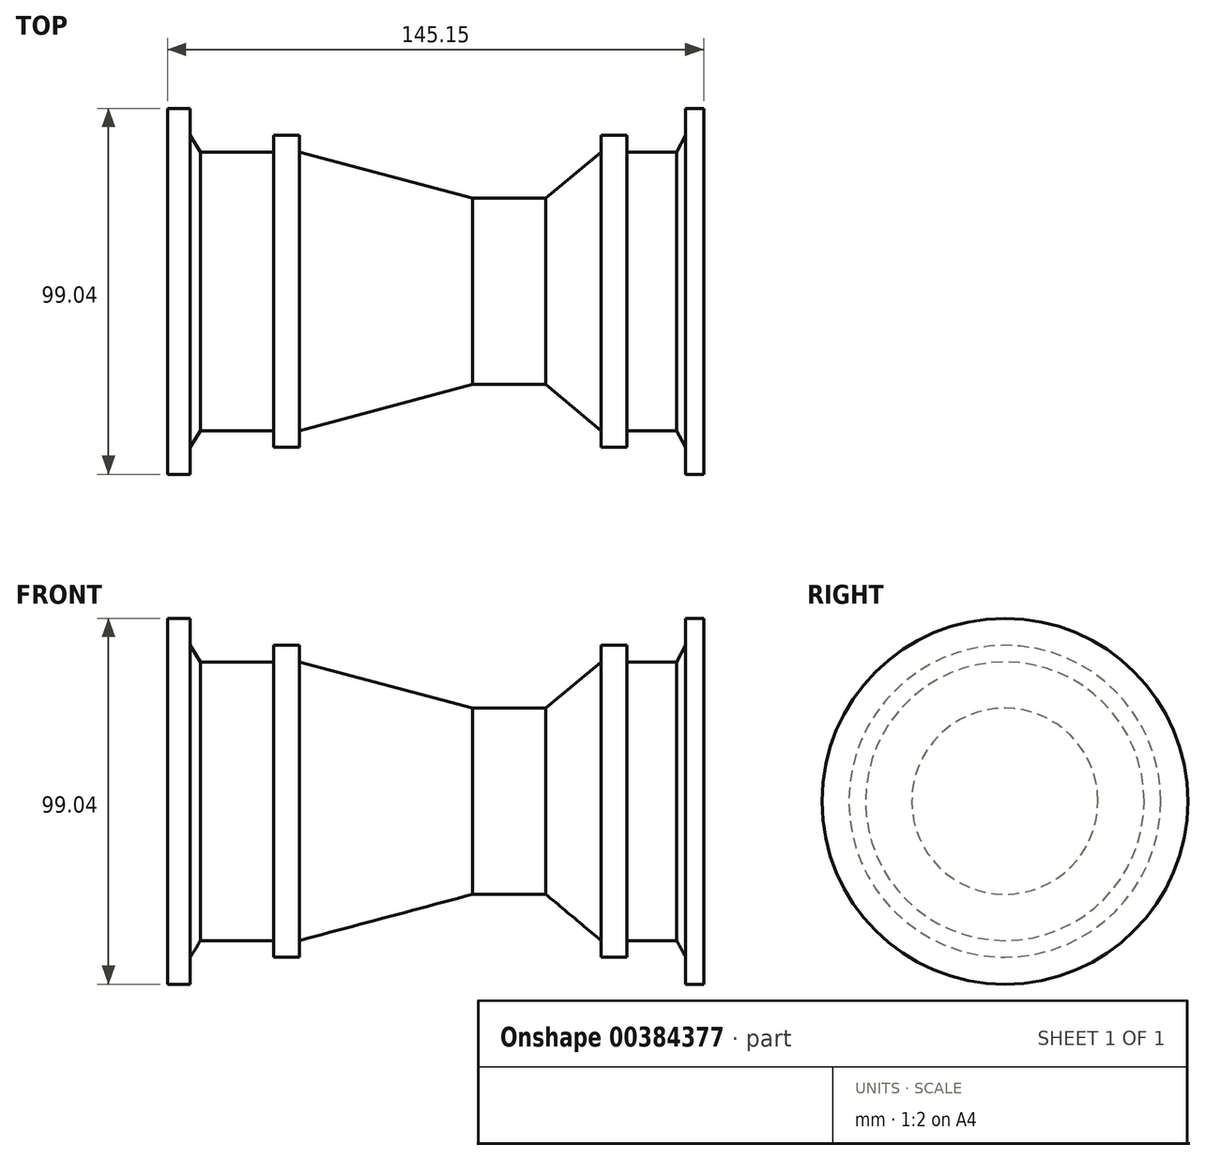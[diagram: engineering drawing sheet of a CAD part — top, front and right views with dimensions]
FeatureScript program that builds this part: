
annotation { "Feature Type Name" : "Feature", "Feature Type Description" : "" }
export const myFeature = defineFeature(function(context is Context, id is Id, definition is map)
    precondition{}
    {
        {
            var Q0;
            Q0=qCreatedBy(makeId("Front.planeOp"),FACE);
            var sketch = newSketch(context, id + "F0", { "sketchPlane" : qUnion([Q0])});
            skLineSegment(sketch, "E0", {"start": v(-72.5, 49.52) * mm, "end": v(-66.34, 49.52) * mm});
            skLineSegment(sketch, "E1", {"start": v(-66.34, 49.52) * mm, "end": v(-66.34, 42.22) * mm});
            skLineSegment(sketch, "E2", {"start": v(-66.34, 42.22) * mm, "end": v(-63.56, 37.7) * mm});
            skLineSegment(sketch, "E3", {"start": v(-63.56, 37.7) * mm, "end": v(-43.75, 37.7) * mm});
            skLineSegment(sketch, "E4", {"start": v(-43.75, 37.7) * mm, "end": v(-43.75, 42.22) * mm});
            skLineSegment(sketch, "E5", {"start": v(-43.75, 42.22) * mm, "end": v(-36.8, 42.22) * mm});
            skLineSegment(sketch, "E6", {"start": v(-36.8, 42.22) * mm, "end": v(-36.8, 37.7) * mm});
            skLineSegment(sketch, "E7", {"start": v(-36.8, 37.7) * mm, "end": v(10.1, 25.2) * mm});
            skLineSegment(sketch, "E8", {"start": v(10.1, 25.2) * mm, "end": v(29.92, 25.2) * mm});
            skLineSegment(sketch, "E9", {"start": v(29.92, 25.2) * mm, "end": v(44.86, 37.7) * mm});
            skLineSegment(sketch, "E10", {"start": v(44.86, 37.7) * mm, "end": v(44.86, 42.22) * mm});
            skLineSegment(sketch, "E11", {"start": v(44.86, 42.22) * mm, "end": v(51.8, 42.22) * mm});
            skLineSegment(sketch, "E12", {"start": v(51.8, 42.22) * mm, "end": v(51.8, 37.7) * mm});
            skLineSegment(sketch, "E13", {"start": v(67.8, 42.22) * mm, "end": v(67.8, 49.52) * mm});
            skLineSegment(sketch, "E14", {"start": v(67.8, 49.52) * mm, "end": v(72.66, 49.52) * mm});
            skLineSegment(sketch, "E15", {"start": v(72.66, 49.52) * mm, "end": v(72.66, 0) * mm});
            skLineSegment(sketch, "E16", {"start": v(72.66, 0) * mm, "end": v(-72.5, 0) * mm});
            skLineSegment(sketch, "E17", {"start": v(-72.5, 0) * mm, "end": v(-72.5, 49.52) * mm});
            skLineSegment(sketch, "E18", {"start": v(51.8, 37.7) * mm, "end": v(65.33, 37.7) * mm});
            skLineSegment(sketch, "E19", {"start": v(65.33, 37.7) * mm, "end": v(67.8, 42.22) * mm});
            skSolve(sketch);
        }
        {
            var Q0;
            Q0=makeQuery(id+"F0.imprint","IMPRINT",FACE,{"disambiguationData":[TD([[makeQuery(id+"F0.imprint","IMPRINT",EDGE,{"derivedFrom":sQuery(id+"F0.wireOp",EDGE,"E0")}),-1.0]])]});
            var Q1;
            Q1=sQuery(id+"F0.wireOp",EDGE,"E16");
            revolve(context, id + "F1", {"entities" : qUnion([Q0]), "axis" : qUnion([Q1]), "revolveType" : RevolveType.FULL});
        }
    });
